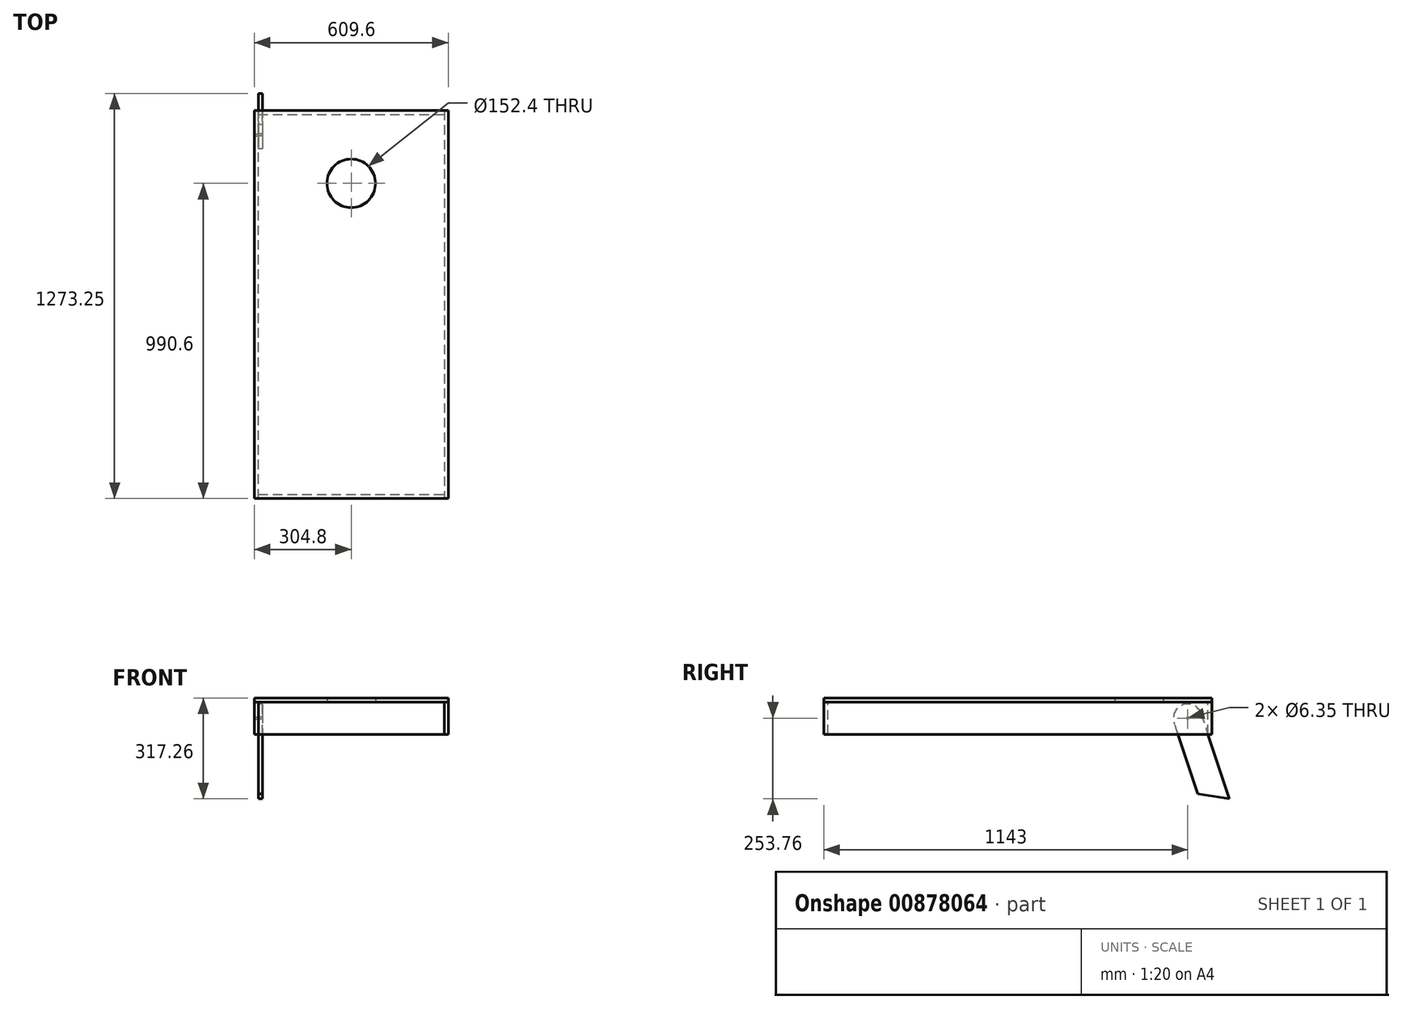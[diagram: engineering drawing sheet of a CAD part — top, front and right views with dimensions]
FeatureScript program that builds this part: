
annotation { "Feature Type Name" : "Feature", "Feature Type Description" : "" }
export const myFeature = defineFeature(function(context is Context, id is Id, definition is map)
    precondition{}
    {
        {
            var Q0;
            Q0=qCreatedBy(makeId("Top.planeOp"),FACE);
            var sketch = newSketch(context, id + "F0", { "sketchPlane" : qUnion([Q0])});
            skLineSegment(sketch, "E0.bottom", {"start": v(304.8, 609.6) * mm, "end": v(-304.8, 609.6) * mm});
            skLineSegment(sketch, "E0.top", {"start": v(304.8, -609.6) * mm, "end": v(-304.8, -609.6) * mm});
            skLineSegment(sketch, "E0.left", {"start": v(304.8, 609.6) * mm, "end": v(304.8, -609.6) * mm});
            skLineSegment(sketch, "E0.right", {"start": v(-304.8, 609.6) * mm, "end": v(-304.8, -609.6) * mm});
            skPoint(sketch, "E0.middle", {"position": v(0, 0) * mm});
            skCircle(sketch, "E1", {"center": v(0, 381) * mm, "radius": 76.2 * mm});
            skSolve(sketch);
        }
        {
            var Q0;
            Q0 = qSketchRegion(id + "F0", true);
            extrude(context, id + "F1", {"entities" : qUnion([Q0]), "depth" : 12.7 * mm, "offsetDistance" : 25.4 * mm});
        }
        {
            var Q0;
            Q0=makeQuery(id+"F1.opExtrude","CAP_FACE",FACE,{"disambiguationData":[OSD([sQuery(id+"F0.wireOp",EDGE,"E0.bottom"),sQuery(id+"F0.wireOp",EDGE,"E0.top"),sQuery(id+"F0.wireOp",EDGE,"E0.left"),sQuery(id+"F0.wireOp",EDGE,"E0.right"),sQuery(id+"F0.wireOp",EDGE,"E1")])],"isStart":true});
            var sketch = newSketch(context, id + "F2", { "sketchPlane" : qUnion([Q0])});
            skLineSegment(sketch, "E2.bottom", {"start": v(-304.8, 609.6) * mm, "end": v(-292.1, 609.6) * mm});
            skLineSegment(sketch, "E2.top", {"start": v(-304.8, -609.6) * mm, "end": v(-292.1, -609.6) * mm});
            skLineSegment(sketch, "E2.left", {"start": v(-304.8, 609.6) * mm, "end": v(-304.8, -609.6) * mm});
            skLineSegment(sketch, "E2.right", {"start": v(-292.1, 609.6) * mm, "end": v(-292.1, -609.6) * mm});
            skLineSegment(sketch, "E3.bottom", {"start": v(304.8, -609.6) * mm, "end": v(292.1, -609.6) * mm});
            skLineSegment(sketch, "E3.top", {"start": v(304.8, 609.6) * mm, "end": v(292.1, 609.6) * mm});
            skLineSegment(sketch, "E3.left", {"start": v(304.8, -609.6) * mm, "end": v(304.8, 609.6) * mm});
            skLineSegment(sketch, "E3.right", {"start": v(292.1, -609.6) * mm, "end": v(292.1, 609.6) * mm});
            skLineSegment(sketch, "E4.bottom", {"start": v(-292.1, 596.9) * mm, "end": v(292.1, 596.9) * mm});
            skLineSegment(sketch, "E4.top", {"start": v(-292.1, 609.6) * mm, "end": v(292.1, 609.6) * mm});
            skLineSegment(sketch, "E4.left", {"start": v(-292.1, 596.9) * mm, "end": v(-292.1, 609.6) * mm});
            skLineSegment(sketch, "E4.right", {"start": v(292.1, 596.9) * mm, "end": v(292.1, 609.6) * mm});
            skLineSegment(sketch, "E5.bottom", {"start": v(-292.1, -609.6) * mm, "end": v(292.1, -609.6) * mm});
            skLineSegment(sketch, "E5.top", {"start": v(-292.1, -596.9) * mm, "end": v(292.1, -596.9) * mm});
            skLineSegment(sketch, "E5.left", {"start": v(-292.1, -609.6) * mm, "end": v(-292.1, -596.9) * mm});
            skLineSegment(sketch, "E5.right", {"start": v(292.1, -609.6) * mm, "end": v(292.1, -596.9) * mm});
            skSolve(sketch);
        }
        {
            var Q0;
            Q0=makeQuery(id+"F2.imprint","IMPRINT",FACE,{"disambiguationData":[TD([[makeQuery(id+"F2.imprint","IMPRINT",EDGE,{"derivedFrom":sQuery(id+"F2.wireOp",EDGE,"E2.bottom")}),1.0]])]});
            var Q1;
            Q1=makeQuery(id+"F2.imprint","IMPRINT",FACE,{"disambiguationData":[TD([[makeQuery(id+"F2.imprint","IMPRINT",EDGE,{"derivedFrom":sQuery(id+"F2.wireOp",EDGE,"E3.bottom")}),-1.0]])]});
            extrude(context, id + "F3", {"entities" : qUnion([Q0, Q1]), "depth" : 101.6 * mm, "offsetDistance" : 25.4 * mm});
        }
        {
            var Q0;
            Q0=makeQuery(id+"F2.imprint","IMPRINT",FACE,{"disambiguationData":[TD([[makeQuery(id+"F2.imprint","IMPRINT",EDGE,{"derivedFrom":sQuery(id+"F2.wireOp",EDGE,"E4.bottom")}),1.0]])]});
            var Q1;
            Q1=makeQuery(id+"F2.imprint","IMPRINT",FACE,{"disambiguationData":[TD([[makeQuery(id+"F2.imprint","IMPRINT",EDGE,{"derivedFrom":sQuery(id+"F2.wireOp",EDGE,"E5.bottom")}),-1.0]])]});
            extrude(context, id + "F4", {"entities" : qUnion([Q0, Q1]), "depth" : 101.6 * mm, "offsetDistance" : 25.4 * mm});
        }
        {
            var Q0;
            Q0=makeQuery(id+"F3.opExtrude","SWEPT_FACE",FACE,{"disambiguationData":[OSD([sQuery(id+"F2.wireOp",EDGE,"E2.right"),sQuery(id+"F2.wireOp",EDGE,"E4.left"),sQuery(id+"F2.wireOp",EDGE,"E5.left")])]});
            var sketch = newSketch(context, id + "F5", { "sketchPlane" : qUnion([Q0])});
            skCircle(sketch, "E6", {"center": v(533.4, -50.8) * mm, "radius": 44.45 * mm});
            skLineSegment(sketch, "E7", {"start": v(575.62, -36.91) * mm, "end": v(663.65, -304.56) * mm});
            skLineSegment(sketch, "E8", {"start": v(663.65, -304.56) * mm, "end": v(564.9, -288.82) * mm});
            skLineSegment(sketch, "E9", {"start": v(564.9, -288.82) * mm, "end": v(491.18, -64.69) * mm});
            skLineSegment(sketch, "E10", {"start": v(-609.6, -101.6) * mm, "end": v(663.65, -304.56) * mm, "construction": true});
            skLineSegment(sketch, "E11.0.1", {"start": v(-609.6, 12.7) * mm, "end": v(609.6, 12.7) * mm, "construction": true});
            skLineSegment(sketch, "E11.0.3", {"start": v(609.6, 12.7) * mm, "end": v(-609.6, 12.7) * mm, "construction": true});
            skCircle(sketch, "E12", {"center": v(533.4, -50.8) * mm, "radius": 3.18 * mm});
            skLineSegment(sketch, "E13", {"start": v(609.6, 12.7) * mm, "end": v(561.62, -288.3) * mm, "construction": true});
            skLineSegment(sketch, "E14", {"start": v(519.51, -8.58) * mm, "end": v(354.86, -62.73) * mm, "construction": true});
            skSolve(sketch);
        }
        {
            var Q0;
            Q0 = qSketchRegion(id + "F5", true);
            extrude(context, id + "F6", {"entities" : qUnion([Q0]), "depth" : 12.7 * mm, "offsetDistance" : 25.4 * mm});
        }
        {
            var Q0;
            Q0=makeQuery(id+"F3.opExtrude","SWEPT_FACE",FACE,{"disambiguationData":[OSD([sQuery(id+"F2.wireOp",EDGE,"E2.right"),sQuery(id+"F2.wireOp",EDGE,"E4.left"),sQuery(id+"F2.wireOp",EDGE,"E5.left")])]});
            var sketch = newSketch(context, id + "F7", { "sketchPlane" : qUnion([Q0])});
            skCircle(sketch, "E15.0", {"center": v(533.4, -50.8) * mm, "radius": 3.18 * mm});
            skSolve(sketch);
        }
        {
            var Q0;
            Q0 = qSketchRegion(id + "F7", true);
            extrude(context, id + "F8", {"entities" : qUnion([Q0]), "operationType" : NewBodyOperationType.REMOVE, "endBound" : BoundingType.THROUGH_ALL, "oppositeDirection" : true, "depth" : 25.4 * mm, "offsetDistance" : 25.4 * mm});
        }
    });
